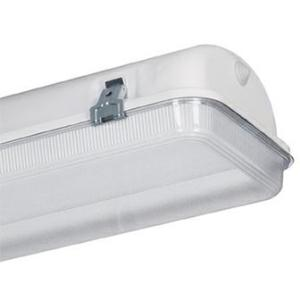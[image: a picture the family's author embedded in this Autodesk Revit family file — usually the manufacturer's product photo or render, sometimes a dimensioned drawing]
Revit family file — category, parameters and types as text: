
# Revit family: 3f_filippi_-_beta_i3f_75_pc_ampio_3f_filippi_-_55600_-_i3f_led_752x30w_ampio_l1565
name_source: partatom
category: Lighting Fixtures
units: mm (PartAtom-declared; Revit-internal decimal feet)

## family parameters
Cut with Voids When Loaded = No
Host = Face
Light Source = No
Part Type = Normal
Room Calculation Point = No
Round Connector Dimension = Use Diameter
Shared = No

## types (1)
- 3F Filippi - Beta i3F 75 PC Ampio (1 x LED, 9715 lm, 66 W, 4000 K)
    Apparent Load = 66 VA
    Approval mark = ENEC
    CIE Flux Codes = 52 82 96 97 100
    Color Rendering = 80
    Color Temperature = 4000 K
    Control Gear = Electronic ballast
    Default Elevation = 1800 mm
    Description = ILLUMINOTECHNICAL
Luminous efficiency 100% (DLOR 97%, ULOR 3%).
Initial luminous flux of the luminaire 9715 lm.
Wide symmetric distribution.
Installation Interdistance Transv.D = 1.27 x hu - Long.D = 1.26 x hu.
Tabular UGR (CIE 117 - 4H-8H; S=0.25H; 70/50/20): RUG 20.6 - 22.4.
Beam angle: 92° - 100°.
Luminous efficacy 147 lm/W.
Lifetime (L93/B10): 30000 h. (tq+25°C)
Lifetime (L90/B10): 50000 h. (tq+25°C)
Lifetime (L85/B10): 80000 h. (tq+25°C)
Lifetime (L80/B10): 100000 h. (tq+25°C)
Lifetime (L85/B10): 50000 h. (tq+35°C)
Sudden decreased luminous flux after 50000 hours: 0% (C0).
Photobiological safety in compliance with IEC/TR 62778: RG0 risk exempt, (IEC 62471).
In compliance with IEC/EN 62722-2-1 - IEC/EN 62717 standards.

SOURCE
2 linear LED modules 30W/840.
Energy efficiency class (UE 2019/2020 - UE 2019/2015): D.
CIE 13.3 Colour rendering index: CRI >80 (R9 <50%).
IES TM-30 Fidelity Index: Rf = 84 Rg = 95.
CCT nominal colour temperature 4000 K.
Colour initial tolerance (MacAdam): SDCM 3.

MECHANICAL
Single-piece housing in pressed steel, powder-coated in white epoxy-polyester.
Diffuser in self-extinguishing V2 polycarbonate, photo-engraved interior, UV stabilised, injection moulded, with smooth outer surface, sealing gasket, hinged opening by means of galvanised steel clips.
Wide flow recuperator, oversized, in specular aluminium with superficial titanium-magnesium treatment, non-iridescent.
Gear-tray unit in hot-galvanised steel, painted in white polyester, fixed to the housing by means of "Ribloc" rapid devices in galvanised steel, hinged opening.
Luminaire with limited surface temperature. - D - (EN 60598-2-24)
Dimensions: 1565x235 mm, height 135 mm. Weight 6.76 kg.
IP65 protection degree.
Mechanical strength to impacts IK10 (20 joule).
Glow-wire test resistance 850°C.

ELECTRICAL
Halogen Free electronic wiring 230V-50/60Hz, power factor 0.97, THD <25%, constant output current, SELV, class I, 1 driver.
Power of the luminaire 66 W.
CE - IEC 60598-1 - EN 60598-1.
SAFE FLICKER: PstLM=<1 and SVM=<0.4 (IEC TR 61547-1 and IEC TR 63158), to ensure a more comfortable and safe light.
Luminaire compliant with EN 60598-2-22 for power supply from a centralised emergency system CPSS (Central Power Supply System), not incorporated in the luminaire - high risk areas excluded. The default power and flux are 100% in AC and 100% in DC.
Ambient temperature from -20°C to +35°C.
Temperature class T6 max 85°C.
Relative humidity UR: <85%.

INSTALLATION
Ceiling / Suspended / Wall.
All accessories dedicated to this product are available on the Catalog and on our website www.3F-Filippi.com.

APPLICATIONS
Suitable product for food production plants (HACCP), IFS (Food Version 6), BRC (GSFS Food Version 7).
In industrial environments, stores and dry, dusty indoor environments, subject to occasional water splashes.

WARNING
Fixture not suitable for cold stores with an ambient temperature <0°C and/or relative humidity >85%.
Luminaire designed for disposal/recycling at end-of-life.
Replaceable (LED only) light source by a professional. Replaceable control gear by a professional.
    Height = 135 mm
    Lamp = 1 x LED
    Lamp Light Flux = 9715 lm
    Lamp Power = 66 W
    Lamp count = 1
    Length = 1565 mm
    Lifetime = 50000 h
    Luminous efficacy = 147 lm/W
    Manufacturer = 3F Filippi
    ModVariant = No
    Model = 3F Filippi - 55600 - i3F LED 752x30W AMPIO L1565
    Mounting Place = Ceiling
    Mounting Type = Pendant
    Number of Poles = 1
    OnlyDefault = Yes
    Power Factor = 1
    Product Name = 3F Filippi - Beta i3F 75 PC Ampio
    Product group = pendant luminaire
    ProductGroupID = 9
    Protection Class = Protection class I
    Protection Degree = IP 65
    RLX_Detail_Level = 1
    RLX_Emergency_Light_Flux = 0 lm
    RLX_Emergency_Type = 0
    RLX_Emergency_Type_DB = No
    RlxData = <blob elided: 67953 chars, md5=a1c015a0>
    Socket = socket
    Standby Power = 0 W
    System Light Flux = 9715 lm
    System Power = 66 W
    Type Comments = Product without accessories
    Type Image = 3ffilippi_55600.jpg
    URL = http://relux.com
    VarID = ---
    Voltage = 0 V
    Weight = 0.00 kg
    Width = 235 mm

## geometry (parser evidence)
native form markers: Blend x4, Sweep x11
no freeform markers — native parametric forms only
